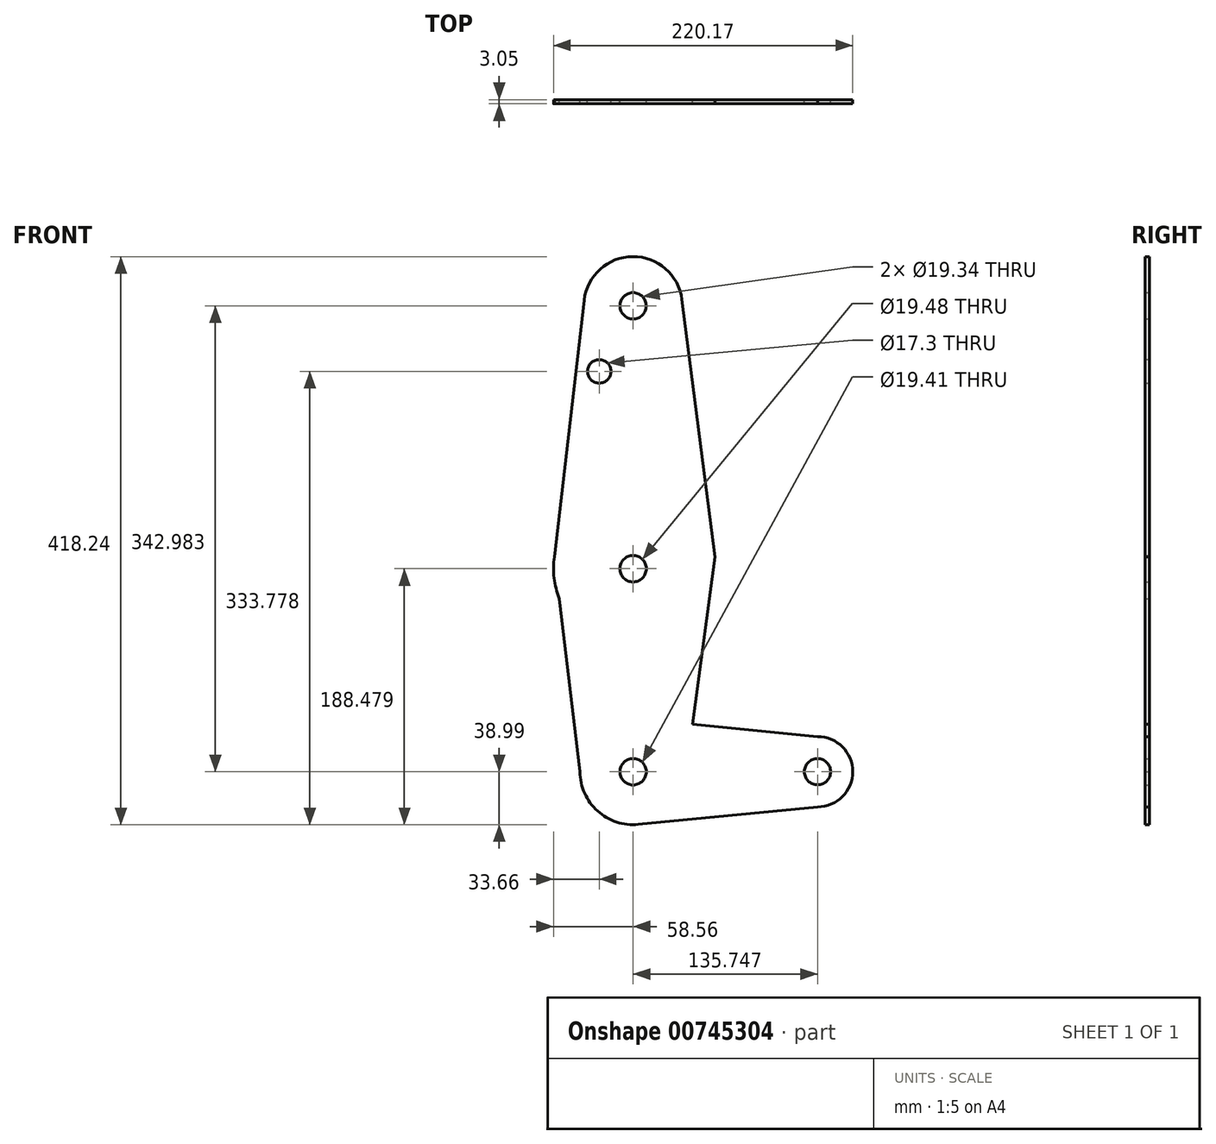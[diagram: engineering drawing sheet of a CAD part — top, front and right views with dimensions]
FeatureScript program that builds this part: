
annotation { "Feature Type Name" : "Feature", "Feature Type Description" : "" }
export const myFeature = defineFeature(function(context is Context, id is Id, definition is map)
    precondition{}
    {
        {
            var Q0;
            Q0=qCreatedBy(makeId("Front.planeOp"),FACE);
            var sketch = newSketch(context, id + "F0", { "sketchPlane" : qUnion([Q0])});
            skCircle(sketch, "E0", {"center": v(0, 0) * mm, "radius": 39 * mm});
            skCircle(sketch, "E1", {"center": v(135.75, 0) * mm, "radius": 25.87 * mm});
            skCircle(sketch, "E2", {"center": v(0, 149.49) * mm, "radius": 58.56 * mm});
            skCircle(sketch, "E3", {"center": v(0, 342.98) * mm, "radius": 36.27 * mm});
            skLineSegment(sketch, "E4", {"start": v(135.75, -25.87) * mm, "end": v(3.8, -38.8) * mm});
            skLineSegment(sketch, "E5", {"start": v(135.75, 25.87) * mm, "end": v(0, 39.18) * mm});
            skLineSegment(sketch, "E6", {"start": v(39, 0) * mm, "end": v(60.27, 158.28) * mm});
            skLineSegment(sketch, "E7", {"start": v(-39, 0) * mm, "end": v(-57.9, 158.28) * mm});
            skLineSegment(sketch, "E8", {"start": v(-57.9, 158.28) * mm, "end": v(-36.03, 347.15) * mm});
            skLineSegment(sketch, "E9", {"start": v(60.27, 158.28) * mm, "end": v(35.97, 347.6) * mm});
            skCircle(sketch, "E10", {"center": v(-24.9, 294.79) * mm, "radius": 8.65 * mm});
            skCircle(sketch, "E11", {"center": v(0, 342.98) * mm, "radius": 9.67 * mm});
            skCircle(sketch, "E12", {"center": v(0, 149.49) * mm, "radius": 9.74 * mm});
            skCircle(sketch, "E13", {"center": v(0, 0) * mm, "radius": 9.7 * mm});
            skCircle(sketch, "E14", {"center": v(135.75, 0) * mm, "radius": 9.67 * mm});
            skSolve(sketch);
        }
        {
            var Q0;
            Q0 = qSketchRegion(id + "F0", true);
            extrude(context, id + "F1", {"entities" : qUnion([Q0]), "depth" : 3.05 * mm, "offsetDistance" : 25.4 * mm});
        }
    });
